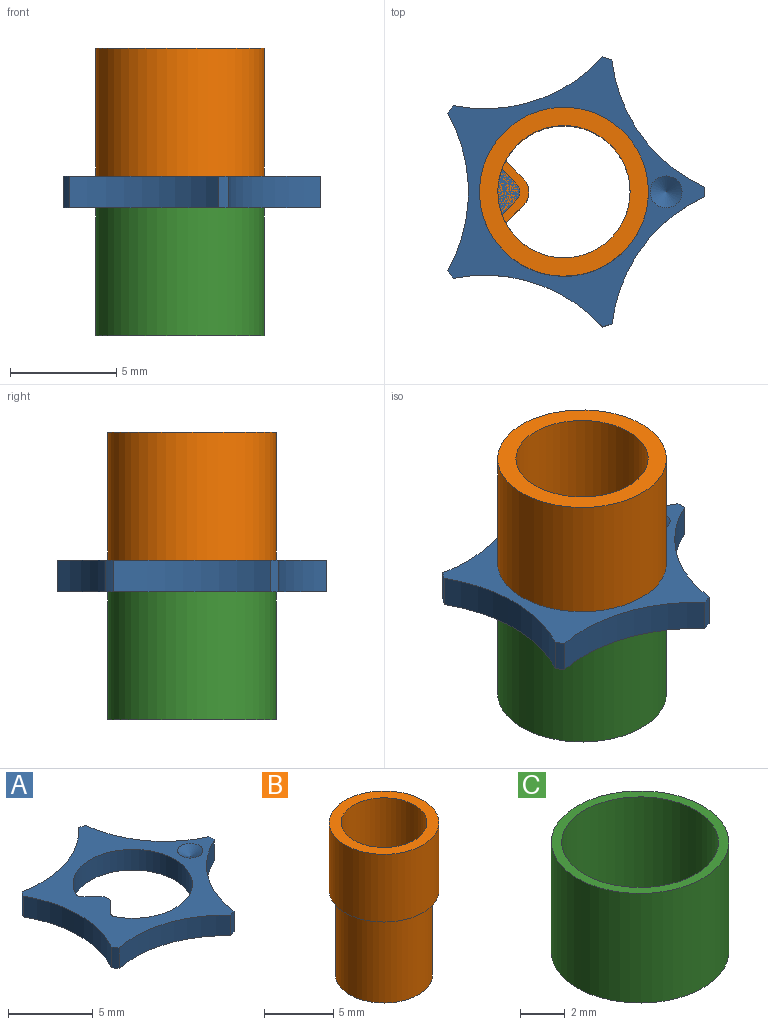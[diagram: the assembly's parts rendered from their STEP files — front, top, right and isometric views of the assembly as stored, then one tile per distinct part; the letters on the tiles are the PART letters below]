
ASSEMBLY  parts=3 mates=1
PART A: 19 faces, bbox 12.1x12.7x1.5 mm
  f0: cylinder r=7.5mm len=7.03mm, axis (0,0,-1), area 11.6mm2, adj f1,f15,f16,f17
  f1: cylinder r=6.6mm len=1.5mm, axis (0,0,-1), area 0.7mm2, adj f0,f2,f16,f17
  f2: cylinder r=7.5mm len=7.39mm, axis (0,0,-1), area 11.6mm2, adj f1,f3,f16,f17
  f3: cylinder r=6.6mm len=1.5mm, axis (0,0,-1), area 0.7mm2, adj f2,f4,f16,f17
  f4: cylinder r=7.5mm len=7.02mm, axis (0,0,-1), area 11.6mm2, adj f3,f5,f16,f17
  f5: cylinder r=6.6mm len=1.5mm, axis (0,0,-1), area 0.7mm2, adj f4,f6,f16,f17
  f6: cylinder r=7.5mm len=5.97mm, axis (0,0,-1), area 11.6mm2, adj f5,f7,f16,f17
  f7: cylinder r=6.6mm len=1.5mm, axis (0,0,-1), area 0.7mm2, adj f6,f8,f16,f17
  f8: cylinder r=7.5mm len=5.98mm, axis (0,0,-1), area 11.6mm2, adj f7,f15,f16,f17
  f9: cylinder r=3.53mm len=7.06mm, axis (0,0,-1), area 28.3mm2, adj f10,f14,f16,f17
  f10: cylinder r=0.3mm len=1.5mm, axis (0,0,-1), area 0.6mm2, adj f9,f11,f16,f17
  f11: plane 1.5x0.83mm, normal (0.71,-0.71,0), area 1.8mm2, adj f10,f12,f16,f17
  f12: cylinder r=0.6mm len=1.5mm, axis (0,0,-1), area 1.4mm2, adj f11,f13,f16,f17
  f13: plane 1.5x0.83mm, normal (0.71,0.71,0), area 1.8mm2, adj f12,f14,f16,f17
  f14: cylinder r=0.3mm len=1.5mm, axis (0,0,-1), area 0.6mm2, adj f9,f13,f16,f17
  f15: cylinder r=6.6mm len=1.5mm, axis (0,0,-1), area 0.7mm2, adj f0,f8,f16,f17
  f16: plane 12.69x12.07mm, normal (0,0,1), area 45.8mm2, adj f0,f1,f2,f3,f4,f5,f6,f7
  f17: plane 12.69x12.07mm, normal (0,0,-1), area 47.6mm2, adj f0,f1,f2,f3,f4,f5,f6,f7
  f18: cone r=0.75mm half-angle=60deg, axis (0,0,1), area 2mm2, adj f16
PART B: 12 faces, bbox 7.9x7.9x13.5 mm
  f0: cylinder r=3.11mm len=13.5mm, axis (0,0,-1), area 239mm2, adj f2,f4,f6,f7,f11
  f1: cylinder r=3.97mm len=7.94mm, axis (0,0,-1), area 149.7mm2, adj f2,f3
  f2: plane 7.94x7.94mm, normal (0,0,1), area 19.2mm2, adj f0,f1
  f3: plane 7.94x7.94mm, normal (0,0,-1), area 10.8mm2, adj f1,f10
  f4: plane 3.13x1.46mm, normal (0,0,1), area 2.7mm2, adj f0,f5,f6,f7,f8,f9
  f5: plane 7.5x0.75mm, normal (0.71,-0.71,0), area 7.9mm2, adj f4,f6,f9,f11
  f6: cylinder r=0.15mm len=7.5mm, axis (0,0,1), area 1.5mm2, adj f0,f4,f5,f11
  f7: cylinder r=0.15mm len=7.5mm, axis (0,0,1), area 1.5mm2, adj f0,f4,f8,f11
  f8: plane 7.5x0.75mm, normal (0.71,0.71,0), area 7.9mm2, adj f4,f7,f9,f11
  f9: cylinder r=0.9mm len=7.5mm, axis (0,0,1), area 10.6mm2, adj f4,f5,f8,f11
  f10: cylinder r=3.51mm len=7.5mm, axis (0,0,1), area 165.4mm2, adj f3,f11
  f11: plane 7.02x7.02mm, normal (0,0,-1), area 11mm2, adj f0,f5,f6,f7,f8,f9,f10
PART C: 4 faces, bbox 7.9x7.9x6 mm
  f0: cylinder r=3.51mm len=7.02mm, axis (0,0,-1), area 132.3mm2, adj f2,f3
  f1: cylinder r=3.97mm len=7.94mm, axis (0,0,-1), area 149.7mm2, adj f2,f3
  f2: plane 7.94x7.94mm, normal (0,0,1), area 10.8mm2, adj f0,f1
  f3: plane 7.94x7.94mm, normal (0,0,-1), area 10.8mm2, adj f0,f1
PLACE A t=(0,0,-1.5)mm
PLACE B at identity fixed
PLACE C t=(0,0,-7.5)mm
MATE fastened A.f1 <-> C.f0  axis (0,0,1) through (0,0,-1.5)mm
